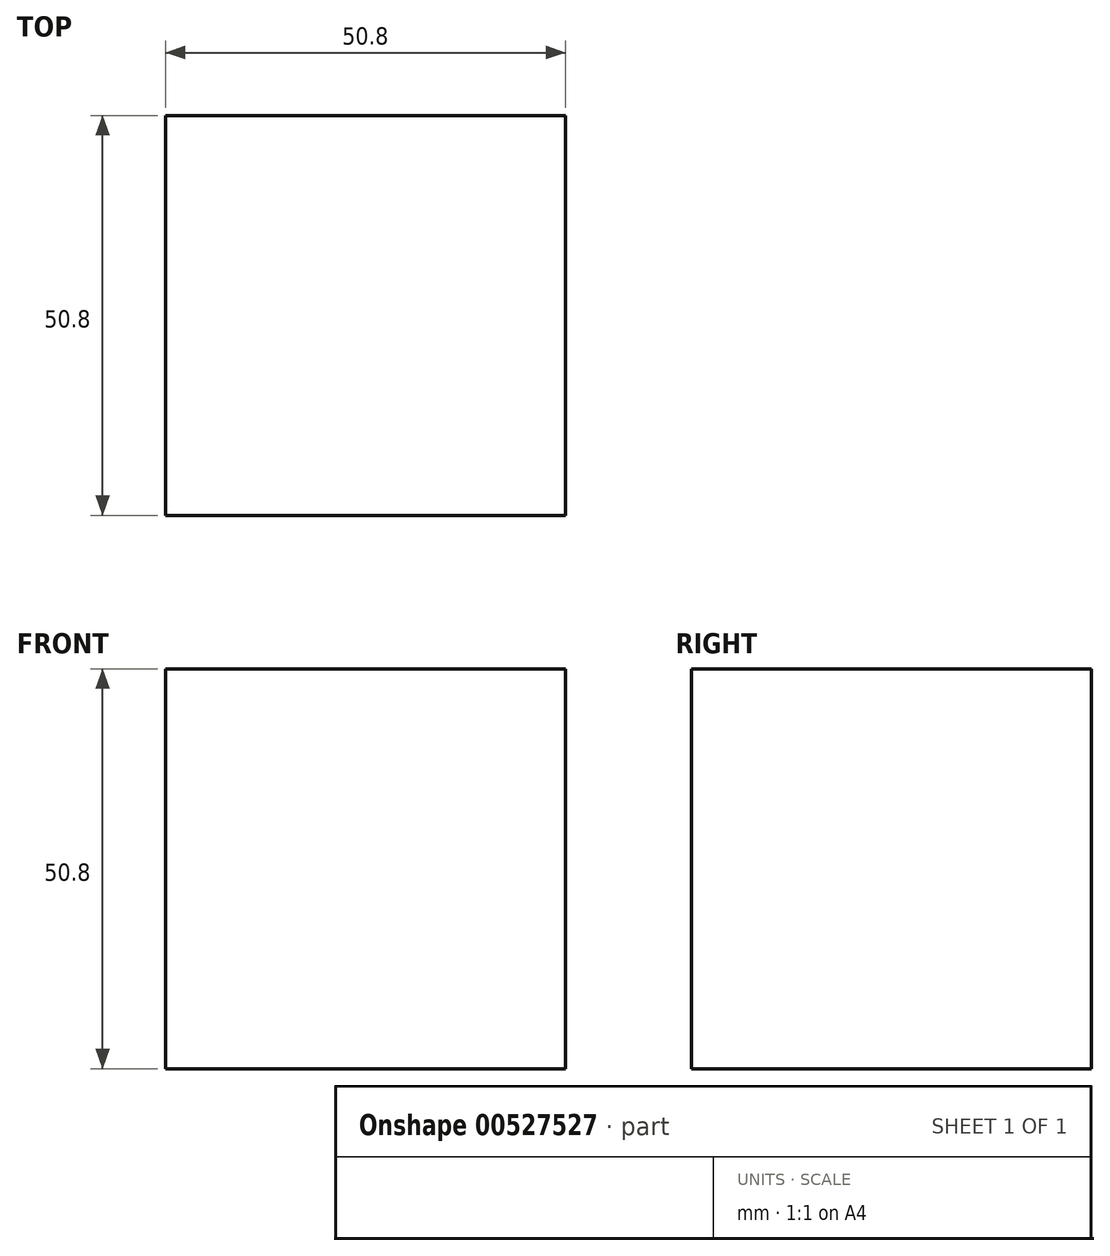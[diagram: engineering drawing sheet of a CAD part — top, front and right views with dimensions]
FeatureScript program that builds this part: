
annotation { "Feature Type Name" : "Feature", "Feature Type Description" : "" }
export const myFeature = defineFeature(function(context is Context, id is Id, definition is map)
    precondition{}
    {
        {
            var Q0;
            Q0=qCreatedBy(makeId("Front.planeOp"),FACE);
            var sketch = newSketch(context, id + "F0", { "sketchPlane" : qUnion([Q0])});
            skLineSegment(sketch, "E0", {"start": v(0, 0) * mm, "end": v(50.8, 0) * mm});
            skLineSegment(sketch, "E1", {"start": v(0, 0) * mm, "end": v(0, 50.8) * mm});
            skLineSegment(sketch, "E2", {"start": v(0, 50.8) * mm, "end": v(50.8, 50.8) * mm});
            skLineSegment(sketch, "E3", {"start": v(50.8, 0) * mm, "end": v(50.8, 50.8) * mm});
            skSolve(sketch);
        }
        {
            var Q0;
            Q0 = qSketchRegion(id + "F0", true);
            extrude(context, id + "F1", {"entities" : qUnion([Q0]), "oppositeDirection" : true, "depth" : 50.8 * mm, "offsetDistance" : 25.4 * mm});
        }
    });
